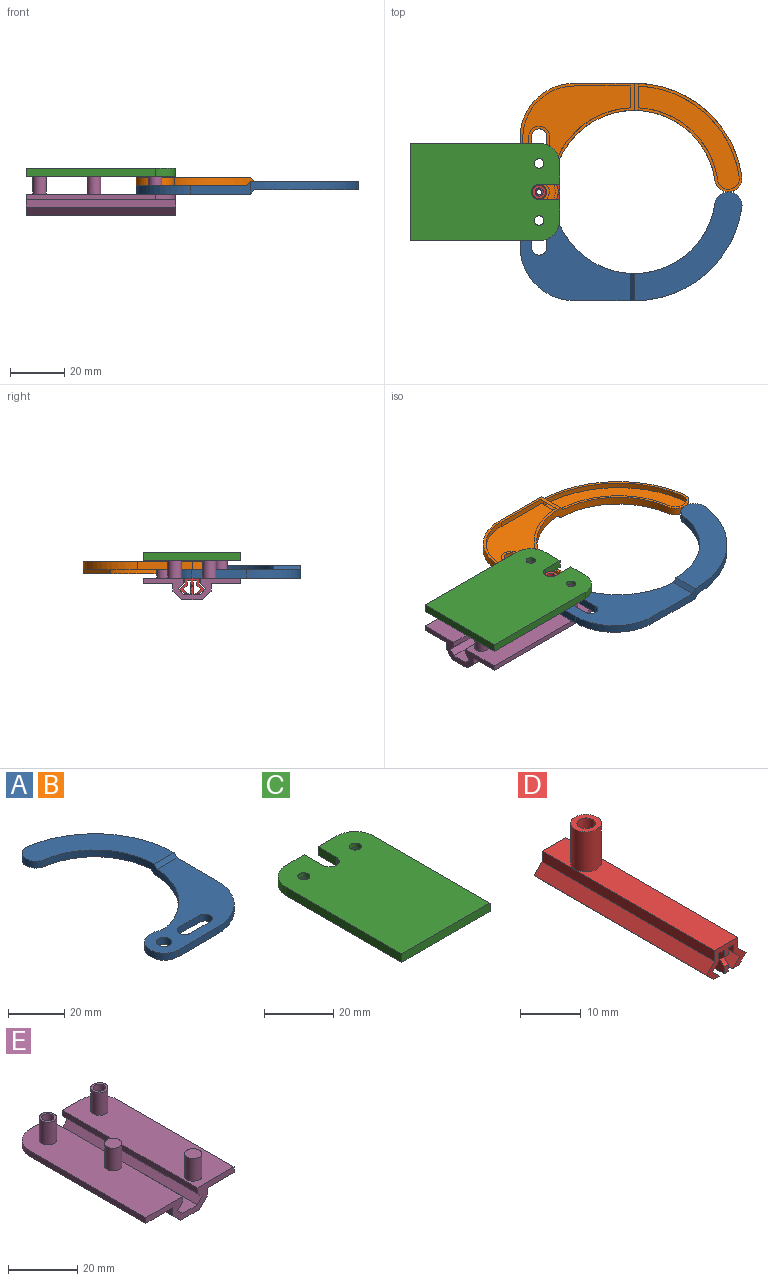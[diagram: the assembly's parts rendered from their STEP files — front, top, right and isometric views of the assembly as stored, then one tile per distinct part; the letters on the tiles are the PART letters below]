
ASSEMBLY  parts=5 mates=7
PART A: 39 faces, bbox 47x81.6x4.5 mm
  f0: plane 7.5x7.5mm, normal (0,0,-1), area 20.4mm2, adj f13,f31
  f1: plane 47x42mm, normal (0,0,-1), area 152.3mm2, adj f7,f8,f9,f10,f11,f12,f19,f25
  f2: plane 17.5x7.5mm, normal (0,0,-1), area 40.4mm2, adj f4,f5,f6,f14,f22,f23,f24,f32
  f3: plane 39.97x38.14mm, normal (0,0,-1), area 111.1mm2, adj f12,f16,f17,f19,f30,f34,f35
  f4: cylinder r=2.75mm len=5.5mm, axis (0,0,-1), area 25.9mm2, adj f2,f5,f14,f15
  f5: plane 10x3mm, normal (0,-1,0), area 30mm2, adj f2,f4,f6,f15
  f6: cylinder r=2.75mm len=5.5mm, axis (0,0,-1), area 25.9mm2, adj f2,f5,f14,f15
  f7: cylinder r=10mm len=6.51mm, axis (0,0,-1), area 19.9mm2, adj f1,f8,f12,f15
  f8: cylinder r=7mm len=14mm, axis (0,0,-1), area 73.5mm2, adj f1,f7,f9,f15
  f9: plane 20x3mm, normal (0,-1,0), area 60mm2, adj f1,f8,f10,f15
  f10: cylinder r=20mm len=20mm, axis (0,0,-1), area 94.2mm2, adj f1,f9,f11,f15
  f11: plane 22x4.5mm, normal (1,0,0), area 67.1mm2, adj f1,f10,f15,f16,f20
  f12: cylinder r=30mm len=58.32mm, axis (0,0,-1), area 244.8mm2, adj f1,f3,f7,f15,f17,f18,f19,f20
  f13: cylinder r=2.75mm len=5.5mm, axis (0,0,-1), area 51.8mm2, adj f0,f15
  f14: plane 10x3mm, normal (0,1,0), area 30mm2, adj f2,f4,f6,f15
  f15: plane 47x40.5mm, normal (0,0,1), area 854.4mm2, adj f4,f5,f6,f7,f8,f9,f10,f11
  f16: cylinder r=40mm len=39.59mm, axis (0,0,-1), area 172.4mm2, adj f3,f11,f17,f18,f19
  f17: cylinder r=5mm len=9.95mm, axis (0,0,-1), area 47.1mm2, adj f3,f12,f16,f18
  f18: plane 40x39.64mm, normal (0,0,1), area 538.9mm2, adj f12,f16,f17,f20
  f19: plane 10.04x1.5mm, normal (0,0.71,-0.71), area 21.2mm2, adj f1,f3,f12,f16,f21
  f20: plane 10.04x1.5mm, normal (0,-0.71,0.71), area 21.2mm2, adj f11,f12,f15,f18
  f21: plane 8.04x1.41mm, normal (0,0,1), area 11.3mm2, adj f19,f30,f34,f37
  f22: cylinder r=3.75mm len=7.5mm, axis (0,0,-1), area 23.6mm2, adj f2,f23,f32,f33
  f23: plane 10x2mm, normal (0,1,0), area 20mm2, adj f2,f22,f24,f33
  f24: cylinder r=3.75mm len=7.5mm, axis (0,0,-1), area 23.6mm2, adj f2,f23,f32,f33
  f25: cylinder r=11mm len=7.16mm, axis (0,0,-1), area 14.6mm2, adj f1,f26,f30,f33
  f26: cylinder r=6mm len=12mm, axis (0,0,-1), area 42mm2, adj f1,f25,f27,f33
  f27: plane 20x2mm, normal (0,1,0), area 40mm2, adj f1,f26,f28,f33
  f28: cylinder r=19mm len=19mm, axis (0,0,-1), area 59.7mm2, adj f1,f27,f29,f33
  f29: plane 22x3.09mm, normal (-1,0,0), area 43.6mm2, adj f1,f28,f33,f34,f37,f38
  f30: cylinder r=31mm len=60.27mm, axis (0,0,-1), area 166.6mm2, adj f1,f3,f21,f25,f33,f35,f36,f37
  f31: cylinder r=3.75mm len=7.5mm, axis (0,0,-1), area 47.1mm2, adj f0,f33
  f32: plane 10x2mm, normal (0,-1,0), area 20mm2, adj f2,f22,f24,f33
  f33: plane 45x39.91mm, normal (0,0,-1), area 658.9mm2, adj f22,f23,f24,f25,f26,f27,f28,f29
  f34: cylinder r=39mm len=38.6mm, axis (0,0,-1), area 111.3mm2, adj f3,f21,f29,f35,f36,f37,f38
  f35: cylinder r=4mm len=7.96mm, axis (0,0,-1), area 25.1mm2, adj f3,f30,f34,f36
  f36: plane 38.23x38mm, normal (0,0,-1), area 421.5mm2, adj f30,f34,f35,f38
  f37: plane 8.03x1.5mm, normal (0,-0.71,0.71), area 17mm2, adj f1,f21,f29,f30,f34
  f38: plane 8.02x1.5mm, normal (0,0.71,-0.71), area 17mm2, adj f29,f30,f33,f34,f36
PART B: same geometry as A
PART C: 22 faces, bbox 36x55x3 mm
  f0: plane 47.5x3mm, normal (-1,0,0), area 142.5mm2, adj f1,f13,f14,f19
  f1: plane 36x3mm, normal (0,-1,0), area 108mm2, adj f0,f2,f14,f19
  f2: plane 47.5x3mm, normal (1,0,0), area 142.5mm2, adj f1,f3,f14,f19
  f3: cylinder r=7.5mm len=7.5mm, axis (0,0,1), area 35.3mm2, adj f2,f4,f14,f19
  f4: plane 7.7x3mm, normal (0,1,0), area 23.1mm2, adj f3,f5,f14,f19
  f5: plane 7.5x3mm, normal (-1,0,0), area 22.5mm2, adj f4,f6,f14,f19
  f6: cylinder r=2.8mm len=5.6mm, axis (0,0,1), area 26.4mm2, adj f5,f7,f14,f19
  f7: plane 7.5x3mm, normal (1,0,0), area 22.5mm2, adj f6,f8,f14,f19
  f8: plane 7.7x3mm, normal (0,1,0), area 23.1mm2, adj f7,f13,f14,f19
  f9: cylinder r=2.8mm len=5.6mm, axis (0,0,1), area 26.4mm2, adj f14,f15
  f10: cylinder r=2.8mm len=5.6mm, axis (0,0,1), area 26.4mm2, adj f14,f16
  f11: cylinder r=2.8mm len=5.6mm, axis (0,0,1), area 26.4mm2, adj f14,f17
  f12: cylinder r=2.8mm len=5.6mm, axis (0,0,1), area 26.4mm2, adj f14,f18
  f13: cylinder r=7.5mm len=7.5mm, axis (0,0,1), area 35.3mm2, adj f0,f8,f14,f19
  f14: plane 55x36mm, normal (0,0,-1), area 1803mm2, adj f0,f1,f2,f3,f4,f5,f6,f7
  f15: plane 5.6x5.6mm, normal (0,0,-1), area 15mm2, adj f9,f21
  f16: plane 5.6x5.6mm, normal (0,0,-1), area 15mm2, adj f10,f20
  f17: plane 5.6x5.6mm, normal (0,0,-1), area 24.6mm2, adj f11
  f18: plane 5.6x5.6mm, normal (0,0,-1), area 24.6mm2, adj f12
  f19: plane 55x36mm, normal (0,0,1), area 1882.3mm2, adj f0,f1,f2,f3,f4,f5,f6,f7
  f20: cylinder r=1.75mm len=3.5mm, axis (0,0,1), area 16.5mm2, adj f16,f19
  f21: cylinder r=1.75mm len=3.5mm, axis (0,0,1), area 16.5mm2, adj f15,f19
PART D: 28 faces, bbox 9.2x40x13.7 mm
  f0: plane 40x3.4mm, normal (0,0,-1), area 121.3mm2, adj f2,f11,f16,f17,f20,f25,f26,f27
  f1: plane 40x1.41mm, normal (0,0,-1), area 56.6mm2, adj f2,f9,f11,f14
  f2: plane 9.15x5.7mm, normal (0,1,0), area 17.6mm2, adj f0,f1,f3,f4,f5,f6,f7,f8
  f3: plane 40x2.12mm, normal (1,0,0), area 85mm2, adj f2,f4,f10,f11
  f4: plane 40x5.4mm, normal (0,0,1), area 196.4mm2, adj f2,f3,f5,f11,f12
  f5: plane 40x2.12mm, normal (-1,0,0), area 85mm2, adj f2,f4,f6,f11
  f6: plane 40x1.88mm, normal (-0.71,0,0.71), area 106.1mm2, adj f2,f5,f7,f11
  f7: plane 40x1.7mm, normal (-0.71,0,-0.71), area 96.2mm2, adj f2,f6,f8,f11
  f8: plane 40x1.41mm, normal (0,0,-1), area 56.6mm2, adj f2,f7,f11,f19
  f9: plane 40x1.7mm, normal (0.71,0,-0.71), area 96.2mm2, adj f1,f2,f10,f11
  f10: plane 40x1.88mm, normal (0.71,0,0.71), area 106.1mm2, adj f2,f3,f9,f11
  f11: plane 9.15x5.7mm, normal (0,-1,0), area 18.9mm2, adj f0,f1,f3,f4,f5,f6,f7,f8
  f12: cylinder r=2.5mm len=8mm, axis (0,0,-1), area 125.7mm2, adj f4,f13
  f13: plane 5x5mm, normal (0,0,1), area 12.6mm2, adj f12,f20
  f14: plane 40x1.7mm, normal (-0.71,0,0.71), area 96.2mm2, adj f1,f2,f11,f15
  f15: plane 40x1.46mm, normal (-0.71,0,-0.71), area 82.7mm2, adj f2,f11,f14,f16
  f16: plane 40x1.54mm, normal (-1,0,0), area 61.5mm2, adj f0,f2,f11,f15
  f17: plane 40x1.54mm, normal (1,0,0), area 61.5mm2, adj f0,f2,f11,f18
  f18: plane 40x1.46mm, normal (0.71,0,-0.71), area 82.7mm2, adj f2,f11,f17,f19
  f19: plane 40x1.7mm, normal (0.71,0,0.71), area 96.2mm2, adj f2,f8,f11,f18
  f20: cylinder r=1.5mm len=9mm, axis (0,0,1), area 84.8mm2, adj f0,f13
  f21: plane 1x1mm, normal (0,-0.71,-0.71), area 1.4mm2, adj f11,f22,f26,f27
  f22: plane 1x1mm, normal (0,-0.71,0.71), area 1.4mm2, adj f21,f23,f26,f27
  f23: plane 1.35x1mm, normal (0,-1,0), area 1.3mm2, adj f22,f24,f26,f27
  f24: plane 2.89x1mm, normal (0,0,-1), area 2.9mm2, adj f23,f25,f26,f27
  f25: plane 4.7x4.7mm, normal (0,0.71,-0.71), area 6.6mm2, adj f0,f24,f26,f27
  f26: plane 7.59x4.7mm, normal (1,0,0), area 23.6mm2, adj f0,f11,f21,f22,f23,f24,f25
  f27: plane 7.59x4.7mm, normal (-1,0,0), area 23.6mm2, adj f0,f11,f21,f22,f23,f24,f25
PART E: 33 faces, bbox 36x55x16 mm
  f0: plane 21x8mm, normal (0,1,0), area 71.9mm2, adj f2,f3,f4,f5,f6,f8,f13,f14
  f1: plane 36x8mm, normal (0,-1,0), area 101.9mm2, adj f2,f3,f4,f8,f13,f14,f15,f16
  f2: plane 55x3.17mm, normal (0.71,0,-0.71), area 246.7mm2, adj f0,f1,f4,f32
  f3: plane 55x15mm, normal (0,0,1), area 773.7mm2, adj f0,f1,f6,f11,f13,f23,f25
  f4: plane 55x7.66mm, normal (0,0,-1), area 418mm2, adj f0,f1,f2,f7,f20
  f5: cylinder r=7.5mm len=7.5mm, axis (0,0,1), area 23.6mm2, adj f0,f8,f22,f24
  f6: cylinder r=7.5mm len=7.5mm, axis (0,0,1), area 23.6mm2, adj f0,f3,f21,f23
  f7: cylinder r=1mm len=2mm, axis (0,0,1), area 12.6mm2, adj f4,f19
  f8: plane 55x15mm, normal (0,0,1), area 773.7mm2, adj f0,f1,f5,f9,f18,f24,f27
  f9: cylinder r=2.5mm len=8mm, axis (0,0,-1), area 125.7mm2, adj f8,f10
  f10: plane 5x5mm, normal (0,0,1), area 10mm2, adj f9,f29
  f11: cylinder r=2.5mm len=8mm, axis (0,0,-1), area 125.7mm2, adj f3,f12
  f12: plane 5x5mm, normal (0,0,1), area 10mm2, adj f11,f30
  f13: plane 55x2mm, normal (1,0,0), area 110mm2, adj f0,f1,f3,f14
  f14: plane 55x2mm, normal (0.71,0,-0.71), area 155.6mm2, adj f0,f1,f13,f15
  f15: plane 55x2mm, normal (0.71,0,0.71), area 155.6mm2, adj f0,f1,f14,f19
  f16: plane 55x2mm, normal (-0.71,0,0.71), area 155.6mm2, adj f0,f1,f17,f19
  f17: plane 55x2mm, normal (-0.71,0,-0.71), area 155.6mm2, adj f0,f1,f16,f18
  f18: plane 55x2mm, normal (-1,0,0), area 110mm2, adj f0,f1,f8,f17
  f19: plane 55x6mm, normal (0,0,1), area 326.9mm2, adj f0,f1,f7,f15,f16
  f20: plane 55x3.17mm, normal (-0.71,0,-0.71), area 246.7mm2, adj f0,f1,f4,f31
  f21: plane 55x11mm, normal (0,0,-1), area 583.3mm2, adj f0,f1,f6,f23,f30,f31
  f22: plane 55x11mm, normal (0,0,-1), area 583.3mm2, adj f0,f1,f5,f24,f29,f32
  f23: plane 47.5x2mm, normal (-1,0,0), area 95mm2, adj f1,f3,f6,f21
  f24: plane 47.5x2mm, normal (1,0,0), area 95mm2, adj f1,f5,f8,f22
  f25: cylinder r=2.5mm len=8mm, axis (0,0,-1), area 125.7mm2, adj f3,f26
  f26: plane 5x5mm, normal (0,0,1), area 19.6mm2, adj f25
  f27: cylinder r=2.5mm len=8mm, axis (0,0,-1), area 125.7mm2, adj f8,f28
  f28: plane 5x5mm, normal (0,0,1), area 19.6mm2, adj f27
  f29: cylinder r=1.75mm len=10mm, axis (0,0,1), area 110mm2, adj f10,f22
  f30: cylinder r=1.75mm len=10mm, axis (0,0,1), area 110mm2, adj f12,f21
  f31: plane 55x2.83mm, normal (-1,0,0), area 155.6mm2, adj f0,f1,f20,f21
  f32: plane 55x2.83mm, normal (1,0,0), area 155.6mm2, adj f0,f1,f2,f22
PLACE A rot(axis=(0,0,-1),90deg) t=(0,0,7.5)mm
PLACE B rot(axis=(-0.71,-0.71,0),180deg) t=(0,0,10.5)mm
PLACE C rot(axis=(0,0,-1),90deg) t=(0,0,7.5)mm
PLACE D rot(axis=(0,0,-1),90deg) t=(0,0,7.43)mm
PLACE E rot(axis=(0,0,-1),90deg) t=(0,0,7.5)mm
MATE planar B.f8 <-> A.f8  axis (0,0,-1) through (0,0,9)mm
MATE cylindrical B.f8 <-> A.f13  axis (0,0,-1) through (0,0,9)mm
MATE pin_slot E.f9 <-> A.f4  axis (0,0,-1) through (0,-10.5,10)mm
MATE slider D.f2 <-> E.f0  axis (1,0,0) through (7.5,0,3.34)mm
MATE cylindrical B.f13 <-> D.f12  axis (0,0,1) through (0,0,12)mm
MATE fastened C.f9 <-> E.f11  axis (0,0,-1) through (0,10.5,14)mm
MATE pin_slot E.f11 <-> B.f6  axis (0,0,-1) through (0,10.5,10)mm
